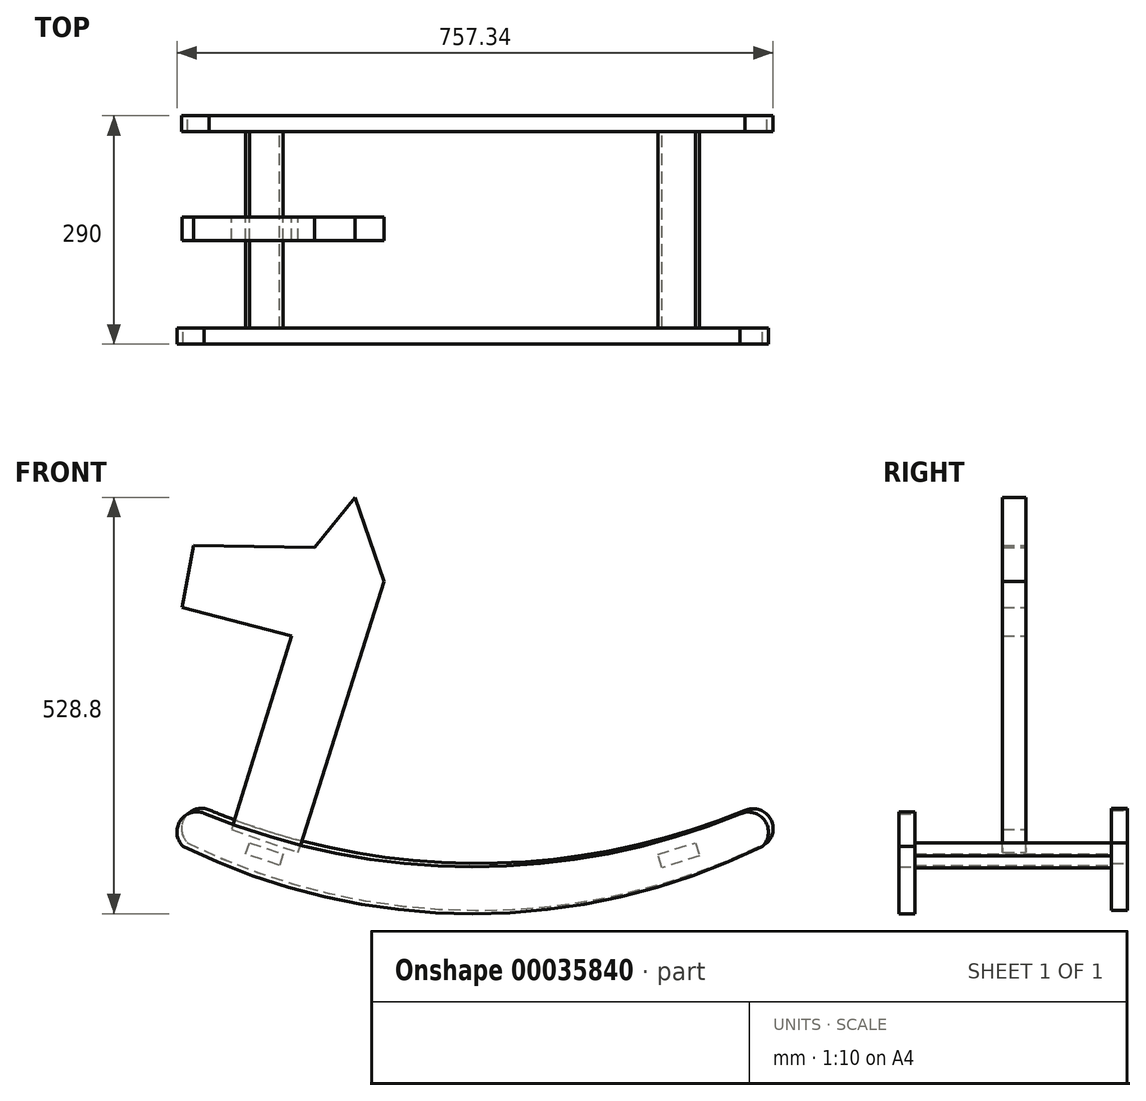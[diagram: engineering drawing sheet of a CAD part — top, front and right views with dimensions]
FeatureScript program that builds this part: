
annotation { "Feature Type Name" : "Feature", "Feature Type Description" : "" }
export const myFeature = defineFeature(function(context is Context, id is Id, definition is map)
    precondition{}
    {
        {
            var Q0;
            Q0=qCreatedBy(makeId("Front.planeOp"),FACE);
            var sketch = newSketch(context, id + "F0", { "sketchPlane" : qUnion([Q0])});
            skArc(sketch, "E0", {"start": v(-365.74, 0) * mm, "mid": v(2.44, -85.81) * mm, "end": v(370.61, 0) * mm});
            skArc(sketch, "E1", {"start": v(-338.52, 41.95) * mm, "mid": v(1.68, -26.1) * mm, "end": v(342.06, 41.05) * mm});
            skArc(sketch, "E2", {"start": v(370.61, 0) * mm, "mid": v(373.53, 32.48) * mm, "end": v(342.06, 41.05) * mm});
            skArc(sketch, "E3", {"start": v(-338.52, 41.95) * mm, "mid": v(-369.27, 32.1) * mm, "end": v(-365.74, 0) * mm});
            skSolve(sketch);
        }
        {
            var Q0;
            Q0=makeQuery(id+"F0.imprint","IMPRINT",FACE,{"disambiguationData":[TD([[makeQuery(id+"F0.imprint","IMPRINT",EDGE,{"derivedFrom":sQuery(id+"F0.wireOp",EDGE,"E0")}),1.0]])]});
            extrude(context, id + "F1", {"entities" : qUnion([Q0]), "depth" : 20 * mm});
        }
        {
            var Q0;
            Q0=makeQuery(id+"F1.opExtrude","CAP_FACE",FACE,{"disambiguationData":[OSD([sQuery(id+"F0.wireOp",EDGE,"E0"),sQuery(id+"F0.wireOp",EDGE,"E1"),sQuery(id+"F0.wireOp",EDGE,"E2"),sQuery(id+"F0.wireOp",EDGE,"E3")])],"isStart":false});
            var sketch = newSketch(context, id + "F2", { "sketchPlane" : qUnion([Q0])});
            skLineSegment(sketch, "E4", {"start": v(-286.87, 0) * mm, "end": v(-244.22, -14.13) * mm});
            skLineSegment(sketch, "E5", {"start": v(-244.22, -14.13) * mm, "end": v(-248.96, -28.45) * mm});
            skLineSegment(sketch, "E6", {"start": v(-248.96, -28.45) * mm, "end": v(-292.19, -14.13) * mm});
            skLineSegment(sketch, "E7", {"start": v(-292.19, -14.13) * mm, "end": v(-286.87, 0) * mm});
            skLineSegment(sketch, "E8", {"start": v(231.86, -14.9) * mm, "end": v(279.22, 0) * mm});
            skLineSegment(sketch, "E9", {"start": v(279.22, 0) * mm, "end": v(284.42, -16.55) * mm});
            skLineSegment(sketch, "E10", {"start": v(284.42, -16.55) * mm, "end": v(236.85, -31.51) * mm});
            skLineSegment(sketch, "E11", {"start": v(236.85, -31.51) * mm, "end": v(231.86, -14.9) * mm});
            skSolve(sketch);
        }
        {
            var Q0;
            Q0 = qSketchRegion(id + "F2", true);
            extrude(context, id + "F3", {"entities" : qUnion([Q0]), "operationType" : NewBodyOperationType.ADD, "depth" : 250 * mm});
        }
        {
            var Q0;
            Q0=makeQuery(id+"F3.opExtrude","CAP_FACE",FACE,{"disambiguationData":[OSD([sQuery(id+"F2.wireOp",EDGE,"E4"),sQuery(id+"F2.wireOp",EDGE,"E5"),sQuery(id+"F2.wireOp",EDGE,"E6"),sQuery(id+"F2.wireOp",EDGE,"E7")])],"isStart":false});
            var sketch = newSketch(context, id + "F4", { "sketchPlane" : qUnion([Q0])});
            skArc(sketch, "E12", {"start": v(-1264.04, 653.2) * mm, "mid": v(-895.87, 567.39) * mm, "end": v(-527.7, 653.2) * mm});
            skArc(sketch, "E13", {"start": v(-1236.83, 695.14) * mm, "mid": v(-896.63, 627.09) * mm, "end": v(-556.24, 694.24) * mm});
            skArc(sketch, "E14", {"start": v(-527.7, 653.2) * mm, "mid": v(-524.78, 685.68) * mm, "end": v(-556.24, 694.24) * mm});
            skArc(sketch, "E15", {"start": v(-1236.83, 695.14) * mm, "mid": v(-1267.58, 685.3) * mm, "end": v(-1264.04, 653.2) * mm});
            skSolve(sketch);
        }
        {
            var Q0;
            Q0 = qSketchRegion(id + "F4", true);
            extrude(context, id + "F5", {"entities" : qUnion([Q0]), "depth" : 20 * mm});
        }
        {
            var Q0;
            Q0=makeQuery(id+"F5.opExtrude","SWEPT_BODY",BODY,{"disambiguationData":[OSD([sQuery(id+"F4.wireOp",EDGE,"E12"),sQuery(id+"F4.wireOp",EDGE,"E13"),sQuery(id+"F4.wireOp",EDGE,"E14"),sQuery(id+"F4.wireOp",EDGE,"E15")])]});
            transform(context, id + "F6", {"entities" : qUnion([Q0]), "transformType" : TransformType.TRANSLATION_3D, "dx" : 892.43 * mm, "dy" : 0 * mm, "dz" : 0 * mm, "makeCopy" : false});
        }
        {
            var Q0;
            Q0=makeQuery(id+"F5.opExtrude","SWEPT_BODY",BODY,{"disambiguationData":[OSD([sQuery(id+"F4.wireOp",EDGE,"E12"),sQuery(id+"F4.wireOp",EDGE,"E13"),sQuery(id+"F4.wireOp",EDGE,"E14"),sQuery(id+"F4.wireOp",EDGE,"E15")])]});
            transform(context, id + "F7", {"entities" : qUnion([Q0]), "transformType" : TransformType.TRANSLATION_3D, "dx" : 0 * mm, "dy" : 0 * mm, "dz" : -642.43 * mm, "makeCopy" : false});
        }
        {
            var Q0;
            Q0=makeQuery(id+"F5.opExtrude","SWEPT_BODY",BODY,{"disambiguationData":[OSD([sQuery(id+"F4.wireOp",EDGE,"E12"),sQuery(id+"F4.wireOp",EDGE,"E13"),sQuery(id+"F4.wireOp",EDGE,"E14"),sQuery(id+"F4.wireOp",EDGE,"E15")])]});
            transform(context, id + "F8", {"entities" : qUnion([Q0]), "transformType" : TransformType.TRANSLATION_3D, "dx" : 0 * mm, "dy" : -10 * mm, "dz" : 0 * mm, "makeCopy" : false});
        }
        {
            var Q0;
            Q0=makeQuery(id+"F5.opExtrude","SWEPT_BODY",BODY,{"disambiguationData":[OSD([sQuery(id+"F4.wireOp",EDGE,"E12"),sQuery(id+"F4.wireOp",EDGE,"E13"),sQuery(id+"F4.wireOp",EDGE,"E14"),sQuery(id+"F4.wireOp",EDGE,"E15")])]});
            transform(context, id + "F9", {"entities" : qUnion([Q0]), "transformType" : TransformType.TRANSLATION_3D, "dx" : 0 * mm, "dy" : 10 * mm, "dz" : -15.07 * mm, "makeCopy" : false});
        }
        {
            var Q0;
            Q0=qCreatedBy(makeId("Front.planeOp"),FACE);
            var sketch = newSketch(context, id + "F10", { "sketchPlane" : qUnion([Q0])});
            skLineSegment(sketch, "E16", {"start": v(-298.62, 44.08) * mm, "end": v(-242.24, 24.7) * mm});
            skLineSegment(sketch, "E17", {"start": v(-242.24, 24.7) * mm, "end": v(-169.43, 254.3) * mm});
            skLineSegment(sketch, "E18", {"start": v(-169.43, 254.3) * mm, "end": v(-194.1, 325.36) * mm});
            skLineSegment(sketch, "E19", {"start": v(-194.1, 325.36) * mm, "end": v(-228.15, 283.08) * mm});
            skLineSegment(sketch, "E20", {"start": v(-228.15, 283.08) * mm, "end": v(-330.91, 284.84) * mm});
            skLineSegment(sketch, "E21", {"start": v(-330.91, 284.84) * mm, "end": v(-340.36, 232.32) * mm});
            skLineSegment(sketch, "E22", {"start": v(-340.36, 232.32) * mm, "end": v(-247.53, 207.92) * mm});
            skLineSegment(sketch, "E23", {"start": v(-247.53, 207.92) * mm, "end": v(-298.62, 44.08) * mm});
            skSolve(sketch);
        }
        {
            var Q0;
            Q0 = qSketchRegion(id + "F10", true);
            extrude(context, id + "F11", {"entities" : qUnion([Q0]), "depth" : 20 * mm});
        }
        {
            var Q0;
            Q0=makeQuery(id+"F11.opExtrude","SWEPT_BODY",BODY,{"disambiguationData":[OSD([sQuery(id+"F10.wireOp",EDGE,"E16"),sQuery(id+"F10.wireOp",EDGE,"E17"),sQuery(id+"F10.wireOp",EDGE,"E18"),sQuery(id+"F10.wireOp",EDGE,"E19"),sQuery(id+"F10.wireOp",EDGE,"E20"),sQuery(id+"F10.wireOp",EDGE,"E21"),sQuery(id+"F10.wireOp",EDGE,"E22"),sQuery(id+"F10.wireOp",EDGE,"E23")])]});
            transform(context, id + "F12", {"entities" : qUnion([Q0]), "transformType" : TransformType.TRANSLATION_3D, "dx" : 0 * mm, "dy" : -138.63 * mm, "dz" : -37 * mm, "makeCopy" : false});
        }
        {
            var Q0;
            Q0=makeQuery(id+"F11.opExtrude","SWEPT_BODY",BODY,{"disambiguationData":[OSD([sQuery(id+"F10.wireOp",EDGE,"E16"),sQuery(id+"F10.wireOp",EDGE,"E17"),sQuery(id+"F10.wireOp",EDGE,"E18"),sQuery(id+"F10.wireOp",EDGE,"E19"),sQuery(id+"F10.wireOp",EDGE,"E20"),sQuery(id+"F10.wireOp",EDGE,"E21"),sQuery(id+"F10.wireOp",EDGE,"E22"),sQuery(id+"F10.wireOp",EDGE,"E23")])]});
            var Q1;
            Q1=makeQuery(id+"F11.opExtrude","CAP_VERTEX",VERTEX,{"disambiguationData":[OSD([sQuery(id+"F10.wireOp",EDGE,"E16"),sQuery(id+"F10.wireOp",EDGE,"E17")])],"isStart":false});
            transform(context, id + "F13", {"entities" : qUnion([Q0]), "transformType" : TransformType.SCALE_UNIFORMLY, "scale" : 1.5, "makeCopy" : false, "scalePoint" : qUnion([Q1])});
        }
        {
            var Q0;
            Q0=makeQuery(id+"F11.opExtrude","SWEPT_BODY",BODY,{"disambiguationData":[OSD([sQuery(id+"F10.wireOp",EDGE,"E16"),sQuery(id+"F10.wireOp",EDGE,"E17"),sQuery(id+"F10.wireOp",EDGE,"E18"),sQuery(id+"F10.wireOp",EDGE,"E19"),sQuery(id+"F10.wireOp",EDGE,"E20"),sQuery(id+"F10.wireOp",EDGE,"E21"),sQuery(id+"F10.wireOp",EDGE,"E22"),sQuery(id+"F10.wireOp",EDGE,"E23")])]});
            var Q1;
            Q1=makeQuery(id+"F11.opExtrude","CAP_VERTEX",VERTEX,{"disambiguationData":[OSD([sQuery(id+"F10.wireOp",EDGE,"E16"),sQuery(id+"F10.wireOp",EDGE,"E17")])],"isStart":false});
            transform(context, id + "F14", {"entities" : qUnion([Q0]), "transformType" : TransformType.TRANSLATION_3D, "dx" : 16.94 * mm, "dy" : 0 * mm, "dz" : 0 * mm, "makeCopy" : false});
        }
    });
